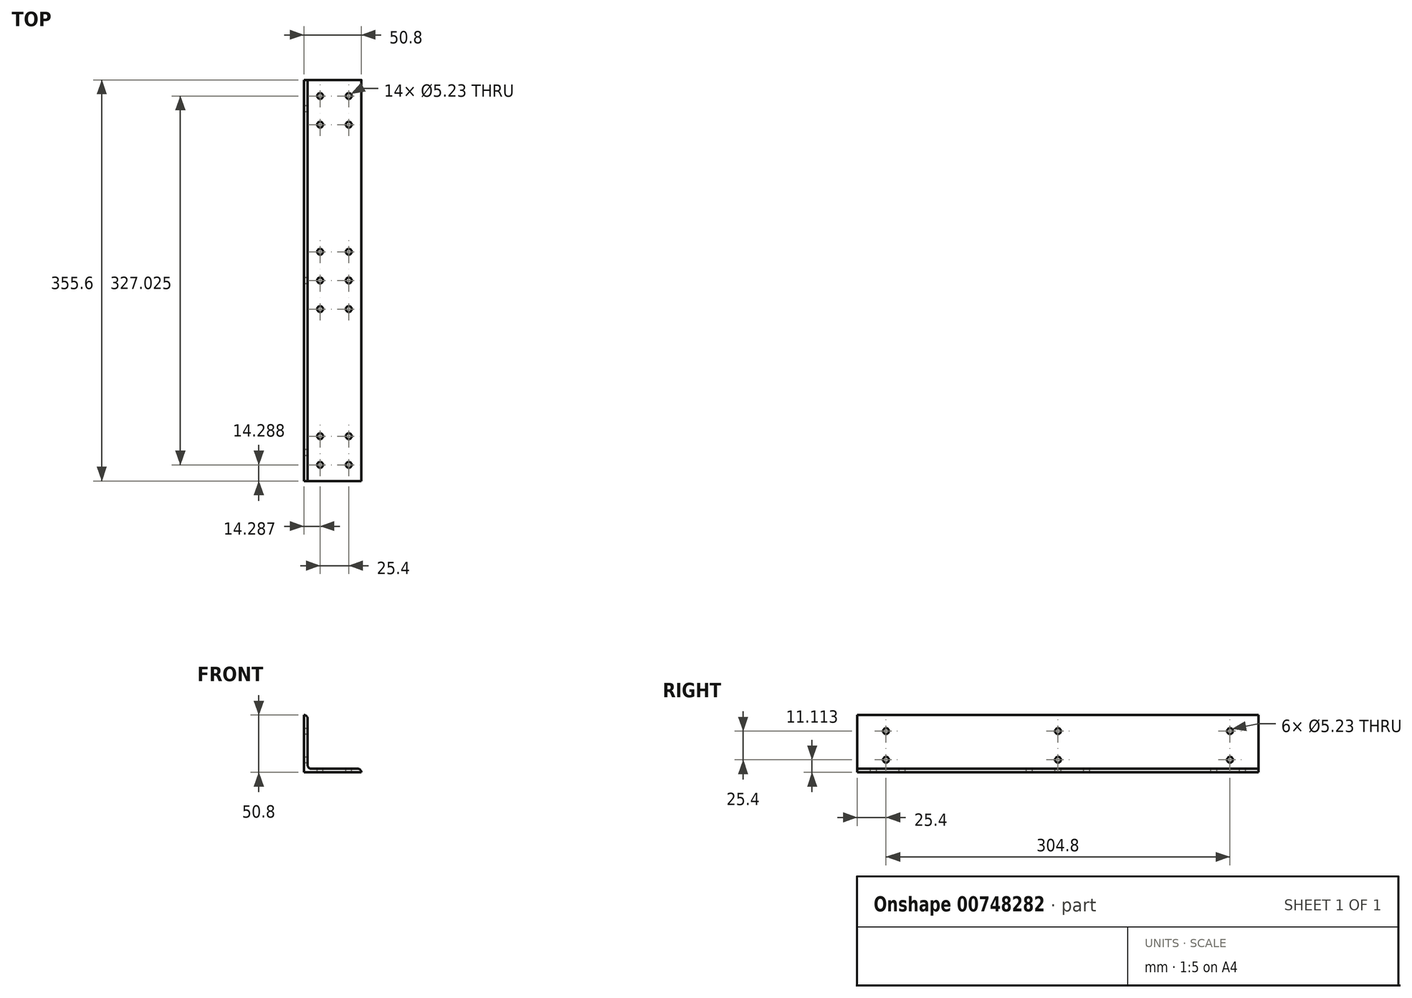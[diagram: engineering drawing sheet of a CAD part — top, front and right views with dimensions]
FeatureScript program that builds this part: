
annotation { "Feature Type Name" : "Feature", "Feature Type Description" : "" }
export const myFeature = defineFeature(function(context is Context, id is Id, definition is map)
    precondition{}
    {
        {
            var Q0;
            Q0=qCreatedBy(makeId("Front.planeOp"),FACE);
            var sketch = newSketch(context, id + "F0", { "sketchPlane" : qUnion([Q0])});
            skLineSegment(sketch, "E0", {"start": v(0, 0) * mm, "end": v(-50.8, 0) * mm});
            skLineSegment(sketch, "E1", {"start": v(-50.8, 0) * mm, "end": v(-50.8, 50.8) * mm});
            skLineSegment(sketch, "E2", {"start": v(-50.8, 50.8) * mm, "end": v(-50.8, 50.8) * mm});
            skLineSegment(sketch, "E3", {"start": v(-47.63, 47.63) * mm, "end": v(-47.63, 6.35) * mm});
            skLineSegment(sketch, "E4", {"start": v(-44.45, 3.18) * mm, "end": v(-3.18, 3.18) * mm});
            skLineSegment(sketch, "E5", {"start": v(0, 0) * mm, "end": v(0, 0) * mm});
            skPoint(sketch, "E6.visualSharp", {"position": v(-47.63, 3.18) * mm});
            skArc(sketch, "E6.filletArc", {"start": v(-47.63, 6.35) * mm, "mid": v(-46.7, 4.1) * mm, "end": v(-44.45, 3.18) * mm});
            skPoint(sketch, "E7.visualSharp", {"position": v(-47.63, 50.8) * mm});
            skArc(sketch, "E7.filletArc", {"start": v(-47.63, 47.63) * mm, "mid": v(-48.55, 49.87) * mm, "end": v(-50.8, 50.8) * mm});
            skPoint(sketch, "E8.visualSharp", {"position": v(0, 3.18) * mm});
            skArc(sketch, "E8.filletArc", {"start": v(0, 0) * mm, "mid": v(-0.93, 2.25) * mm, "end": v(-3.18, 3.18) * mm});
            skSolve(sketch);
        }
        {
            var Q0;
            Q0=qSketchRegion(id+"F0",true);
            extrude(context, id + "F1", {"entities" : qUnion([Q0]), "depth" : 355.6 * mm, "offsetDistance" : 25.4 * mm});
        }
        {
            var Q0;
            Q0=makeQuery(id+"F1.opExtrude","SWEPT_FACE",FACE,{"disambiguationData":[OSD([sQuery(id+"F0.wireOp",EDGE,"E3")])]});
            var sketch = newSketch(context, id + "F2", { "sketchPlane" : qUnion([Q0])});
            skLineSegment(sketch, "E9", {"start": v(-177.8, 6.35) * mm, "end": v(-177.8, 47.62) * mm, "construction": true});
            skLineSegment(sketch, "E10.0", {"start": v(-330.2, 6.35) * mm, "end": v(-330.2, 47.62) * mm, "construction": true});
            skLineSegment(sketch, "E11.0", {"start": v(-25.4, 6.35) * mm, "end": v(-25.4, 47.62) * mm, "construction": true});
            skLineSegment(sketch, "E12", {"start": v(-355.6, 26.99) * mm, "end": v(0, 26.99) * mm, "construction": true});
            skCircle(sketch, "E13", {"center": v(-330.2, 11.11) * mm, "radius": 2.62 * mm});
            skCircle(sketch, "E14", {"center": v(-177.8, 11.11) * mm, "radius": 2.62 * mm});
            skCircle(sketch, "E15", {"center": v(-25.4, 11.11) * mm, "radius": 2.62 * mm});
            skLineSegment(sketch, "E16.0", {"start": v(-355.6, 11.11) * mm, "end": v(0, 11.11) * mm, "construction": true});
            skLineSegment(sketch, "E17", {"start": v(0, 36.51) * mm, "end": v(-355.6, 36.51) * mm, "construction": true});
            skCircle(sketch, "E18", {"center": v(-330.2, 36.51) * mm, "radius": 2.62 * mm});
            skCircle(sketch, "E19", {"center": v(-177.8, 36.51) * mm, "radius": 2.62 * mm});
            skCircle(sketch, "E20", {"center": v(-25.4, 36.51) * mm, "radius": 2.62 * mm});
            skSolve(sketch);
        }
        {
            var Q0;
            Q0=qSketchRegion(id+"F2",true);
            extrude(context, id + "F3", {"entities" : qUnion([Q0]), "operationType" : NewBodyOperationType.REMOVE, "endBound" : BoundingType.THROUGH_ALL, "oppositeDirection" : true, "depth" : 25.4 * mm, "offsetDistance" : 25.4 * mm});
        }
        {
            var Q0;
            Q0=makeQuery(id+"F1.opExtrude","SWEPT_FACE",FACE,{"disambiguationData":[OSD([sQuery(id+"F0.wireOp",EDGE,"E4")])]});
            var sketch = newSketch(context, id + "F4", { "sketchPlane" : qUnion([Q0])});
            skLineSegment(sketch, "E21", {"start": v(-3.18, -341.31) * mm, "end": v(-44.45, -341.31) * mm, "construction": true});
            skCircle(sketch, "E22", {"center": v(-36.51, -341.31) * mm, "radius": 2.62 * mm});
            skLineSegment(sketch, "E23", {"start": v(-44.45, -14.29) * mm, "end": v(-3.18, -14.29) * mm, "construction": true});
            skCircle(sketch, "E24", {"center": v(-36.51, -14.29) * mm, "radius": 2.62 * mm});
            skLineSegment(sketch, "E25", {"start": v(-3.18, -177.8) * mm, "end": v(-44.45, -177.8) * mm, "construction": true});
            skLineSegment(sketch, "E26.0", {"start": v(-3.17, -98.43) * mm, "end": v(-19.05, -98.43) * mm, "construction": true});
            skLineSegment(sketch, "E27.0", {"start": v(-3.17, -257.18) * mm, "end": v(-19.05, -257.18) * mm, "construction": true});
            skCircle(sketch, "E28", {"center": v(-36.51, -177.8) * mm, "radius": 2.62 * mm});
            skLineSegment(sketch, "E29", {"start": v(-23.81, -355.6) * mm, "end": v(-23.81, 0) * mm, "construction": true});
            skLineSegment(sketch, "E30", {"start": v(-36.51, -355.6) * mm, "end": v(-36.51, 0) * mm, "construction": true});
            skLineSegment(sketch, "E31", {"start": v(-11.11, 0) * mm, "end": v(-11.11, -355.6) * mm, "construction": true});
            skCircle(sketch, "E32", {"center": v(-11.11, -341.31) * mm, "radius": 2.62 * mm});
            skCircle(sketch, "E33", {"center": v(-11.11, -177.8) * mm, "radius": 2.62 * mm});
            skCircle(sketch, "E34", {"center": v(-11.11, -14.29) * mm, "radius": 2.62 * mm});
            skLineSegment(sketch, "E35", {"start": v(-44.45, -203.2) * mm, "end": v(-3.18, -203.2) * mm, "construction": true});
            skCircle(sketch, "E36", {"center": v(-36.51, -203.2) * mm, "radius": 2.62 * mm});
            skCircle(sketch, "E37", {"center": v(-11.11, -203.2) * mm, "radius": 2.62 * mm});
            skLineSegment(sketch, "E38", {"start": v(-44.45, -152.4) * mm, "end": v(-3.18, -152.4) * mm, "construction": true});
            skCircle(sketch, "E39", {"center": v(-36.51, -152.4) * mm, "radius": 2.62 * mm});
            skCircle(sketch, "E40", {"center": v(-11.11, -152.4) * mm, "radius": 2.62 * mm});
            skLineSegment(sketch, "E41", {"start": v(-3.18, -39.69) * mm, "end": v(-44.45, -39.69) * mm, "construction": true});
            skCircle(sketch, "E42", {"center": v(-11.11, -39.69) * mm, "radius": 2.62 * mm});
            skCircle(sketch, "E43", {"center": v(-36.51, -39.69) * mm, "radius": 2.62 * mm});
            skLineSegment(sketch, "E44", {"start": v(-3.18, -315.91) * mm, "end": v(-44.45, -315.91) * mm, "construction": true});
            skCircle(sketch, "E45", {"center": v(-11.11, -315.91) * mm, "radius": 2.62 * mm});
            skCircle(sketch, "E46", {"center": v(-36.51, -315.91) * mm, "radius": 2.62 * mm});
            skSolve(sketch);
        }
        {
            var Q0;
            Q0=qSketchRegion(id+"F4",true);
            extrude(context, id + "F5", {"entities" : qUnion([Q0]), "operationType" : NewBodyOperationType.REMOVE, "endBound" : BoundingType.THROUGH_ALL, "oppositeDirection" : true, "depth" : 25.4 * mm, "offsetDistance" : 25.4 * mm});
        }
    });
